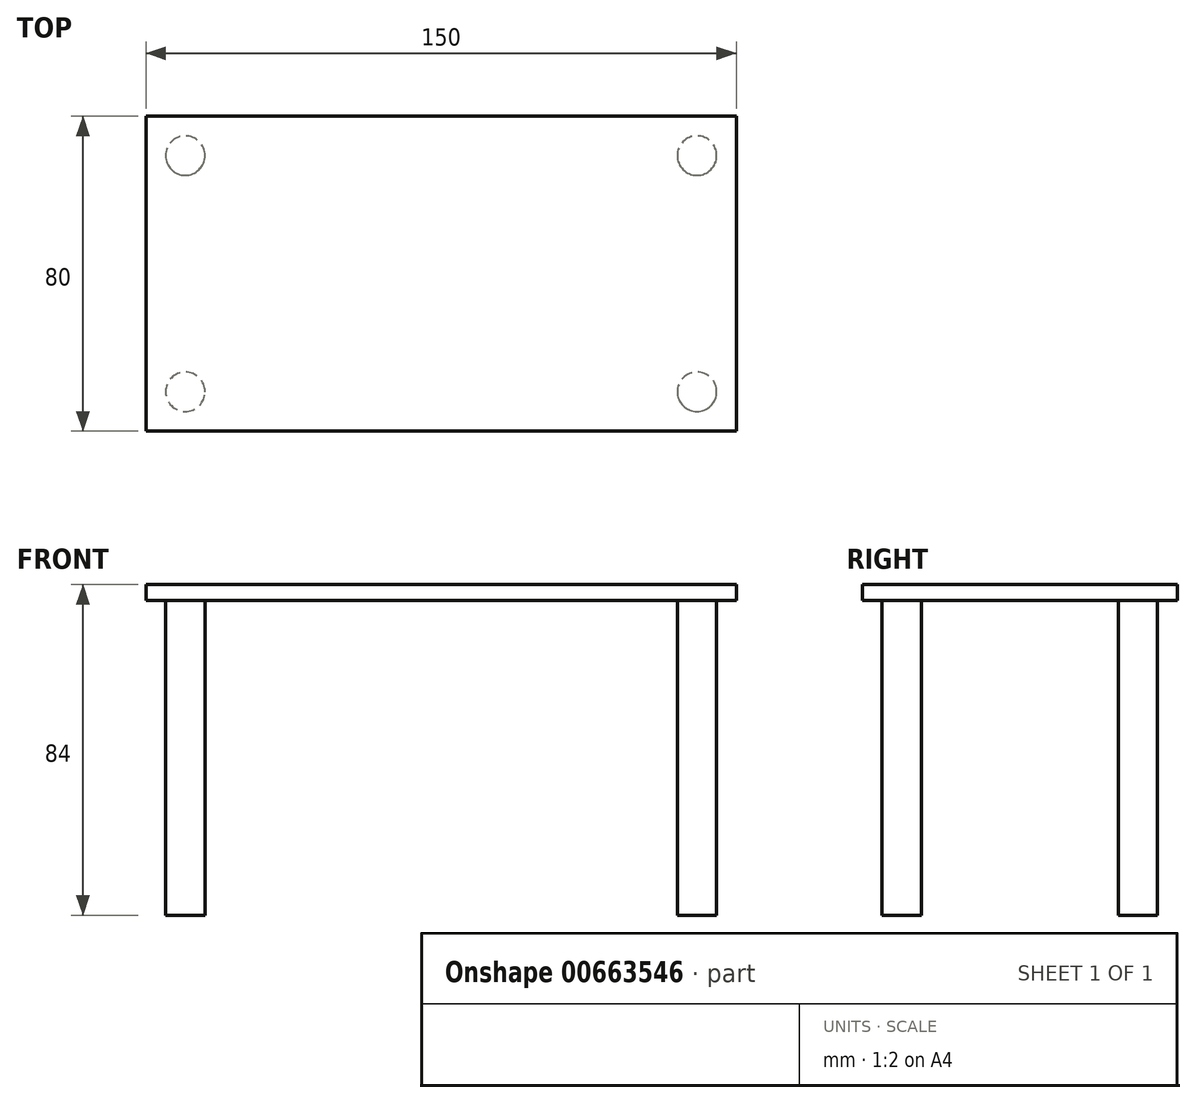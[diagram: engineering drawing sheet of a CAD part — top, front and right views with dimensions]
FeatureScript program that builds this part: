
annotation { "Feature Type Name" : "Feature", "Feature Type Description" : "" }
export const myFeature = defineFeature(function(context is Context, id is Id, definition is map)
    precondition{}
    {
        {
            var Q0;
            Q0=qCreatedBy(makeId("Top.planeOp"),FACE);
            var sketch = newSketch(context, id + "F0", { "sketchPlane" : qUnion([Q0])});
            skLineSegment(sketch, "E0.bottom", {"start": v(-75, 40) * mm, "end": v(75, 40) * mm});
            skLineSegment(sketch, "E0.top", {"start": v(-75, -40) * mm, "end": v(75, -40) * mm});
            skLineSegment(sketch, "E0.left", {"start": v(-75, 40) * mm, "end": v(-75, -40) * mm});
            skLineSegment(sketch, "E0.right", {"start": v(75, 40) * mm, "end": v(75, -40) * mm});
            skPoint(sketch, "E0.middle", {"position": v(0, 0) * mm});
            skSolve(sketch);
        }
        {
            var Q0;
            Q0=makeQuery(id+"F0.imprint","IMPRINT",FACE,{"disambiguationData":[TD([[makeQuery(id+"F0.imprint","IMPRINT",EDGE,{"derivedFrom":sQuery(id+"F0.wireOp",EDGE,"E0.bottom")}),-1.0]])]});
            extrude(context, id + "F1", {"entities" : qUnion([Q0]), "depth" : 4 * mm, "offsetDistance" : 25 * mm});
        }
        {
            var Q0;
            Q0=makeQuery(id+"F1.opExtrude","CAP_FACE",FACE,{"disambiguationData":[OSD([sQuery(id+"F0.wireOp",EDGE,"E0.bottom"),sQuery(id+"F0.wireOp",EDGE,"E0.top"),sQuery(id+"F0.wireOp",EDGE,"E0.left"),sQuery(id+"F0.wireOp",EDGE,"E0.right")])],"isStart":true});
            var sketch = newSketch(context, id + "F2", { "sketchPlane" : qUnion([Q0])});
            skLineSegment(sketch, "E1", {"start": v(-75, 40) * mm, "end": v(-65, 40) * mm, "construction": true});
            skLineSegment(sketch, "E2", {"start": v(-65, 40) * mm, "end": v(-65, 30) * mm, "construction": true});
            skCircle(sketch, "E3", {"center": v(-65, 30) * mm, "radius": 5 * mm});
            skCircle(sketch, "E4.MirrorC", {"center": v(65, 30) * mm, "radius": 5 * mm});
            skCircle(sketch, "E5.MirrorC", {"center": v(65, -30) * mm, "radius": 5 * mm});
            skCircle(sketch, "E6.MirrorC", {"center": v(-65, -30) * mm, "radius": 5 * mm});
            skSolve(sketch);
        }
        {
            var Q0;
            Q0 = qSketchRegion(id + "F2", true);
            extrude(context, id + "F3", {"entities" : qUnion([Q0]), "operationType" : NewBodyOperationType.ADD, "depth" : 80 * mm, "offsetDistance" : 25 * mm});
        }
    });
